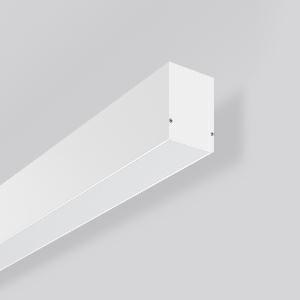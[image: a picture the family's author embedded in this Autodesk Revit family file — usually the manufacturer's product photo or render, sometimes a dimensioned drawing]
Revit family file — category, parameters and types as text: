
# Revit family: less_is_more_50_312609_002_06bd
name_source: partatom
category: Lighting Fixtures
units: mm (PartAtom-declared; Revit-internal decimal feet)

## family parameters
Cut with Voids When Loaded = No
Host = Face
Light Source = No
Part Type = Normal
Room Calculation Point = No
Round Connector Dimension = Use Diameter
Shared = No

## types (1)
- LESS IS MORE 50 (1 x LED Modul 830, 1850 lm, 3000)
    Apparent Load = 15 VA
    CIE Flux Codes = 48 80 96 100 100
    Color Rendering = 80
    Color Temperature = 3000
    Default Elevation = 1800 mm
    Description = Series: LESS IS MORE 50
Linear wall luminaires. Housing: extruded aluminium profile, powder-coated. End cap aluminium powder-coated. Diffuser made of non-yellowing plastic (PMMA), opal. Direct light emission. Suitable for Wall (surface). LED unit with integrated converter interchangeable and removable. Suitable for through-wiring. With sensors or as a safety luminaire on request. 
Colour: traffic white, matt (RAL 9016)
Length: 1407 mm
Width: 67 mm
Height: 75 mm
Lamp: LED
Socket: without socket
Colour temperature: 3000K
Colour rendering index (CRI): 80
System power: 15 W
Rated luminous flux: 1850 lm
Luminous efficiency: 123 lm/W
Control gear: Regulated power supply
Protection class: I
Type of protection: IP 20
    Height = 75 mm
    Lamp = 1 x LED Modul 830
    Lamp Light Flux = 1850 lm
    Lamp count = 1
    Length = 1407 mm
    Lifetime = 50000 h
    Luminous efficacy = 123 lm/W
    Manufacturer = RZB
    ModVariant = No
    Model = 312609.002
    Mounting Place = Wall
    Mounting Type = Surface mounted
    Number of Poles = 1
    OnlyDefault = Yes
    Power Factor = 1
    Product Name = LESS IS MORE 50
    Product group = Surface mounted LED linear luminaires
    ProductGroupID = 2007
    Protection Class = Protection class I
    Protection Degree = IP 20
    RLX_Detail_Level = 1
    RLX_Emergency_Light_Flux = 0 lm
    RLX_Emergency_Type = 0
    RLX_Emergency_Type_DB = No
    RlxData = <blob elided: 35189 chars, md5=ec2087d9>
    Socket = socket
    Standby Power = 0 W
    System Light Flux = 1850 lm
    System Power = 15 W
    Type Comments = Product without accessories
    Type Image = 312606.002.jpg
    URL = http://relux.com
    VarID = ---
    Voltage = 0 V
    Weight = 0.00 kg
    Width = 67 mm

## geometry (parser evidence)
native form markers: Blend x4, Sweep x10
no freeform markers — native parametric forms only
